# Revit family: Series_A_Scale
name_source: partatom
category: Furniture
revit_build: Autodesk Revit 2016 (Build: 20150220_1215(x64)
units: mm (PartAtom-declared; Revit-internal decimal feet)

## family parameters
Always vertical = Yes
Cut with Voids When Loaded = No
OmniClass Number = 23.40.20.00
OmniClass Title = General Furniture and Specialties
Room Calculation Point = No
Shared = No
Work Plane-Based = No

## types (6) — shared parameters
Beam = <By Category>
Dean Unit = <By Category>
Depth = 60"
Description = Series A Scale Conference Table
Height = 28 1/2"
Leg Aprons = <By Category>
Leg Gap 3 = 63"
Levelers = <By Category>
Manufacturer = Poppin, Inc.
Table Ends = <By Category>
Table Top = <By Category>
URL = http://www.poppin.com

## per-type parameters (varying)
| type | End Gap | Leg Gap 1 | Leg Gap 2 | Length | Portion 2 Visibility | Portion 3 Visibility | Table Ends Visibility |
| Series_A_Scale_66 | 66" | 60" | 66" | 66" | No | No | No |
| Series_A_Scale_114 | 66" | 60" | 66" | 114" | No | No | Yes |
| Series_A_Scale_132 | 132" | 63" | 63" | 132" | Yes | No | No |
| Series_A_Scale_180 | 132" | 63" | 63" | 180" | Yes | No | Yes |
| Series_A_Scale_198 | 198" | 63" | 66" | 198" | Yes | Yes | No |
| Series_A_Scale_246 | 198" | 63" | 66" | 246" | Yes | Yes | Yes |

## geometry (parser evidence)
native form markers: Sweep x32
no freeform markers — native parametric forms only
